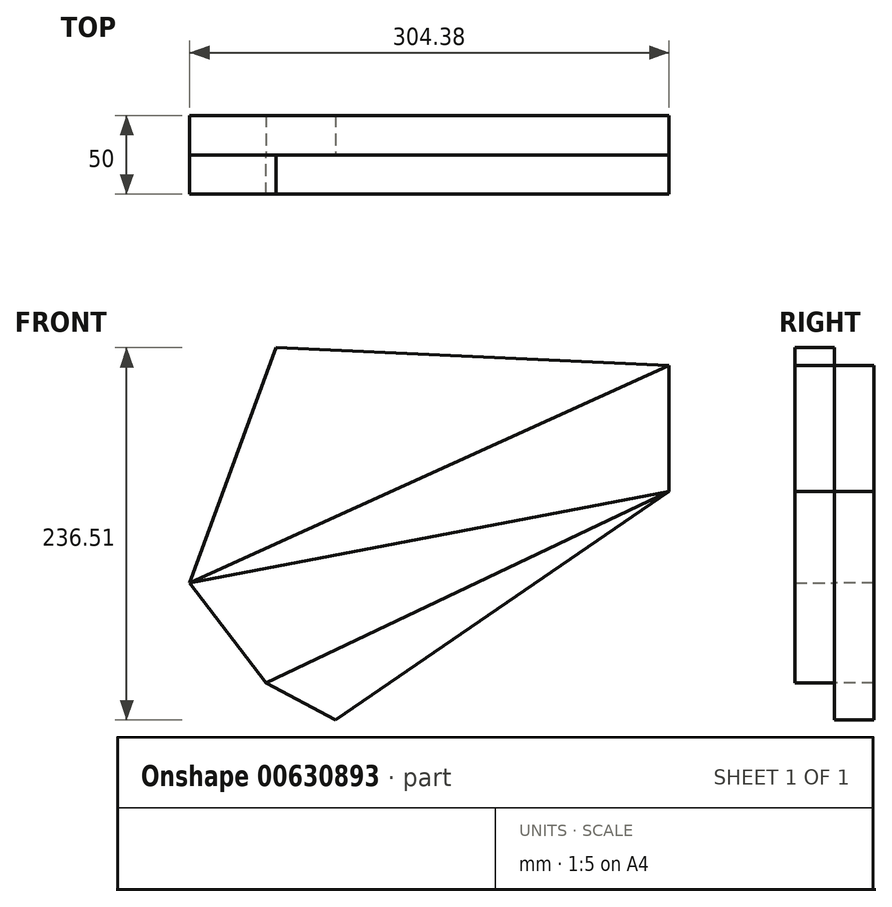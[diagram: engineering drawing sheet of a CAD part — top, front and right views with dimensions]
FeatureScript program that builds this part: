
annotation { "Feature Type Name" : "Feature", "Feature Type Description" : "" }
export const myFeature = defineFeature(function(context is Context, id is Id, definition is map)
    precondition{}
    {
        {
            var Q0;
            Q0=qCreatedBy(makeId("Front.planeOp"),FACE);
            var sketch = newSketch(context, id + "F0", { "sketchPlane" : qUnion([Q0])});
            skLineSegment(sketch, "E0", {"start": v(0, 0) * mm, "end": v(0, 80) * mm});
            skLineSegment(sketch, "E1", {"start": v(0, 80) * mm, "end": v(-249.74, 91.34) * mm});
            skLineSegment(sketch, "E2", {"start": v(-249.74, 91.34) * mm, "end": v(-304.38, -57.98) * mm});
            skLineSegment(sketch, "E3", {"start": v(-304.38, -57.98) * mm, "end": v(0, 80) * mm});
            skLineSegment(sketch, "E4", {"start": v(-304.38, -57.98) * mm, "end": v(0, 0) * mm});
            skLineSegment(sketch, "E5", {"start": v(0, 0) * mm, "end": v(-255.96, -121.65) * mm});
            skLineSegment(sketch, "E6", {"start": v(-304.38, -57.98) * mm, "end": v(-255.96, -121.65) * mm});
            skLineSegment(sketch, "E7", {"start": v(0, 0) * mm, "end": v(-211.83, -145.17) * mm});
            skLineSegment(sketch, "E8", {"start": v(-255.96, -121.65) * mm, "end": v(-211.83, -145.17) * mm});
            skSolve(sketch);
        }
        {
            var Q0;
            Q0=makeQuery(id+"F0.imprint","IMPRINT",FACE,{"disambiguationData":[TD([[makeQuery(id+"F0.imprint","IMPRINT",EDGE,{"derivedFrom":sQuery(id+"F0.wireOp",EDGE,"E1")}),1.0]])]});
            extrude(context, id + "F1", {"entities" : qUnion([Q0]), "depth" : 25 * mm, "offsetDistance" : 25 * mm});
        }
        {
            var Q0;
            Q0=makeQuery(id+"F0.imprint","IMPRINT",FACE,{"disambiguationData":[TD([[makeQuery(id+"F0.imprint","IMPRINT",EDGE,{"derivedFrom":sQuery(id+"F0.wireOp",EDGE,"E0")}),1.0]])]});
            extrude(context, id + "F2", {"entities" : qUnion([Q0]), "operationType" : NewBodyOperationType.ADD, "oppositeDirection" : true, "depth" : 25 * mm, "offsetDistance" : 25 * mm});
        }
        {
            var Q0;
            Q0=makeQuery(id+"F0.imprint","IMPRINT",FACE,{"disambiguationData":[TD([[makeQuery(id+"F0.imprint","IMPRINT",EDGE,{"derivedFrom":sQuery(id+"F0.wireOp",EDGE,"E4")}),-1.0]])]});
            extrude(context, id + "F3", {"entities" : qUnion([Q0]), "depth" : 25 * mm, "offsetDistance" : 25 * mm});
        }
        {
            var Q0;
            Q0=makeQuery(id+"F0.imprint","IMPRINT",FACE,{"disambiguationData":[TD([[makeQuery(id+"F0.imprint","IMPRINT",EDGE,{"derivedFrom":sQuery(id+"F0.wireOp",EDGE,"E5")}),1.0]])]});
            extrude(context, id + "F4", {"entities" : qUnion([Q0]), "operationType" : NewBodyOperationType.ADD, "oppositeDirection" : true, "depth" : 25 * mm, "offsetDistance" : 25 * mm});
        }
    });
